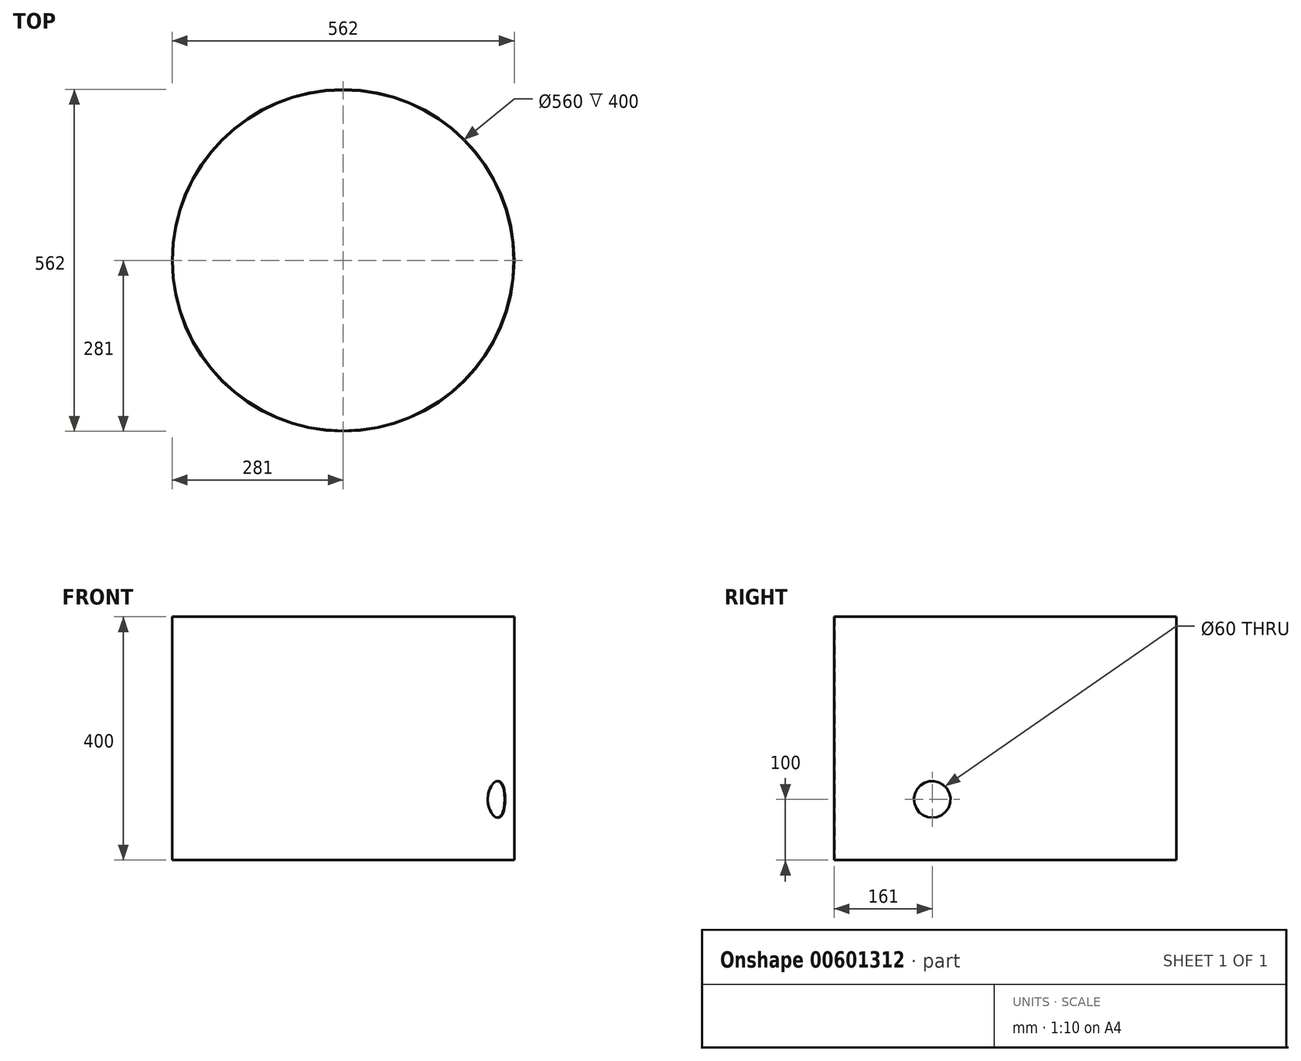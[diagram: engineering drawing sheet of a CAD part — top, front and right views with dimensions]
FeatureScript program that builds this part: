
annotation { "Feature Type Name" : "Feature", "Feature Type Description" : "" }
export const myFeature = defineFeature(function(context is Context, id is Id, definition is map)
    precondition{}
    {
        {
            var Q0;
            Q0=qCreatedBy(makeId("Top.planeOp"),FACE);
            var sketch = newSketch(context, id + "F0", { "sketchPlane" : qUnion([Q0])});
            skCircle(sketch, "E0", {"center": v(0, 0) * mm, "radius": 281 * mm});
            skCircle(sketch, "E1", {"center": v(0, 0) * mm, "radius": 280 * mm});
            skSolve(sketch);
        }
        {
            var Q0;
            Q0=makeQuery(id+"F0.imprint","IMPRINT",FACE,{"disambiguationData":[TD([[makeQuery(id+"F0.imprint","IMPRINT",EDGE,{"derivedFrom":sQuery(id+"F0.wireOp",EDGE,"E0")}),1.0]])]});
            extrude(context, id + "F1", {"entities" : qUnion([Q0]), "endBound" : BoundingType.SYMMETRIC, "depth" : 400 * mm, "offsetDistance" : 25 * mm});
        }
        {
            var Q0;
            Q0=qCreatedBy(makeId("Right.planeOp"),FACE);
            cPlane(context, id + "F2", {"entities" : qUnion([Q0]), "cplaneType" : CPlaneType.OFFSET, "offset" : 281 * mm, "width" : 150 * mm, "height" : 150 * mm});
        }
        {
            var Q0;
            Q0=qCreatedBy(id+"F2.planeOp",FACE);
            var sketch = newSketch(context, id + "F3", { "sketchPlane" : qUnion([Q0])});
            skCircle(sketch, "E2", {"center": v(-120, -100) * mm, "radius": 30 * mm});
            skSolve(sketch);
        }
        {
            var Q0;
            Q0=makeQuery(id+"F3.imprint","IMPRINT",FACE,{"disambiguationData":[TD([[makeQuery(id+"F3.imprint","IMPRINT",EDGE,{"derivedFrom":sQuery(id+"F3.wireOp",EDGE,"E2")}),1.0]])]});
            extrude(context, id + "F4", {"entities" : qUnion([Q0]), "operationType" : NewBodyOperationType.REMOVE, "oppositeDirection" : true, "depth" : 300 * mm, "offsetDistance" : 25 * mm});
        }
    });
